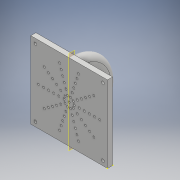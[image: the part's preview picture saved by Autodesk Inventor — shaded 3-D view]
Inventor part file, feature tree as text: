
AUTODESK INVENTOR PART (.ipt)
format: ipt  version: 2018 (Build 220112000, 112)  size: 716,288 bytes
history: native  units: mm
features: sketch x7, extrude x3, pattern_linear x2, pattern_circular x1, plane x1, sweep x1
ambient origin geometry x8: Origin, YZ Plane, XZ Plane, XY Plane, X Axis, Y Axis, Z Axis, Center Point
bodies: Solid1 (feature_tree)
feature tree (15):
  extrude  "Extrusion1"  Depth=150.0mm
  extrude  "Extrusion2"  Depth=4.0mm
  pattern_linear  "Rectangular Pattern1"  Count1=7 Spacing1=10.0mm
  pattern_circular  "Circular Pattern1"  Count=7  [1 undecoded]
  extrude  "Extrusion3"  Depth=12.5mm
  pattern_linear  "Rectangular Pattern2"  Count1=2 Spacing1=132.0mm
  sketch  "Sketch4"  dims[d13=100.0mm d14=360.0deg d16=12.5mm]
  sketch  "Sketch5"  dims[d17=135.0deg]
  sketch  "Sketch6"  dims[d18=10.0mm d19=0.0mm d20=20.0mm d22=132.0mm]
  plane  "Work Plane1"
  sweep  "Sweep1"
  sketch  "Sketch1"  dims[d0=150.0mm d1=150.0mm]
  sketch  "Sketch2"  dims[d2=10.0mm d3=0.0mm d4=4.0mm]
  sketch  "Sketch3"  dims[d5=10.0mm d6=0.0mm d7=70.0mm d9=10.0mm d10=70.0mm d12=10.0mm]
  sketch  "Sketch7"  dims[d23=20.0mm d25=132.0mm d26=-75.0mm d27=0.0mm d28=0.0mm]
note: 1 required parameter value undecoded (feature->parameter linkage not recoverable at this tier; creation-order binding heuristic only, values carry confidence <= 0.55)
